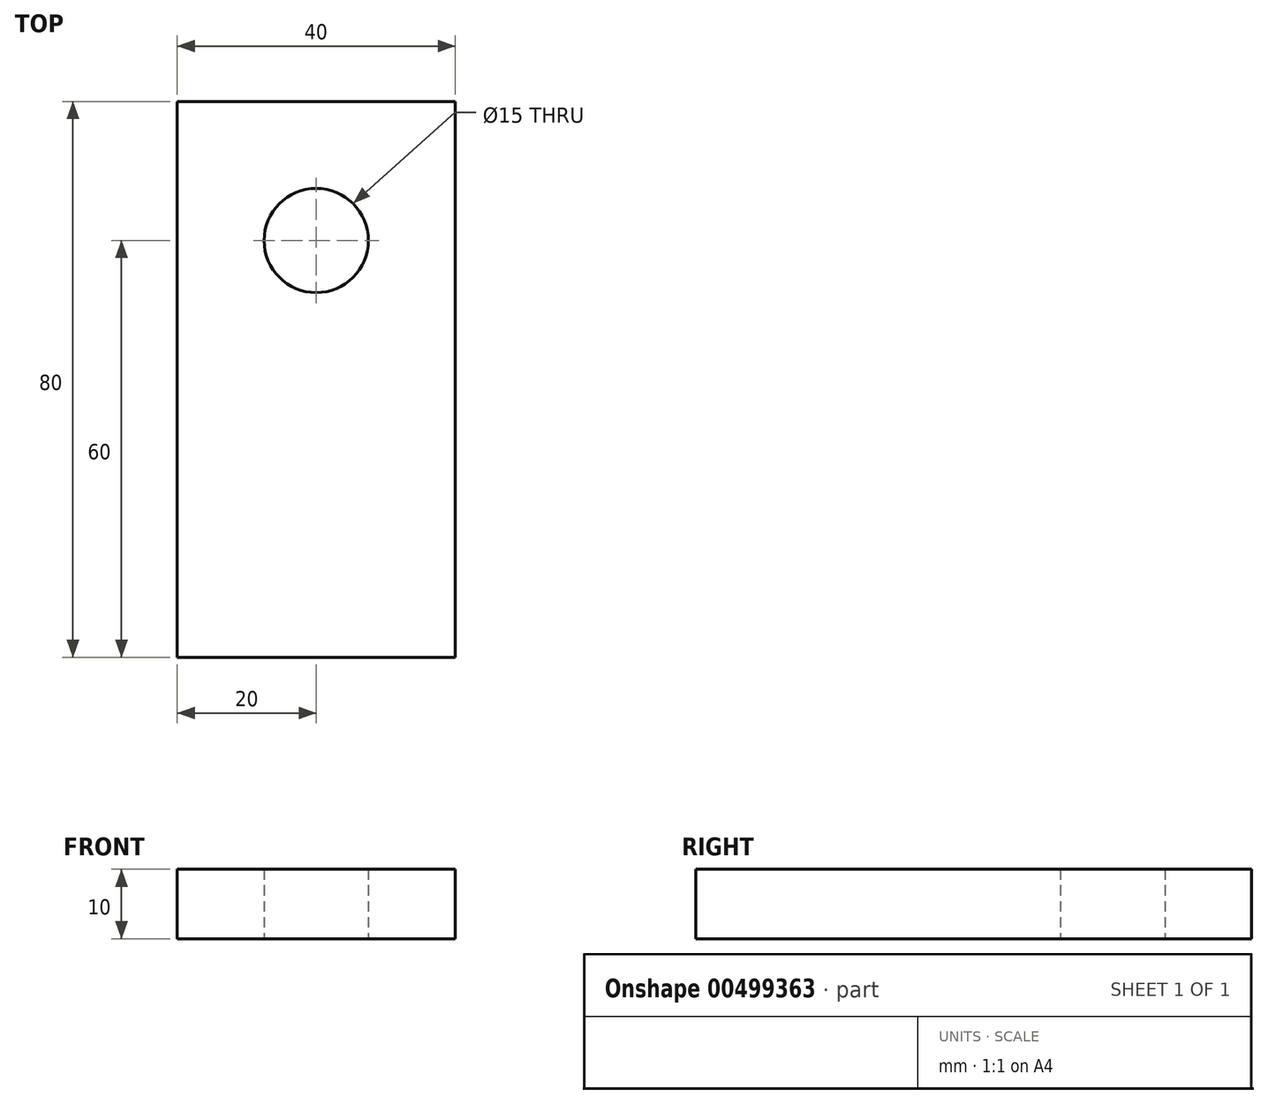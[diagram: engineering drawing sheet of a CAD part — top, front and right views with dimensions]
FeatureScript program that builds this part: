
annotation { "Feature Type Name" : "Feature", "Feature Type Description" : "" }
export const myFeature = defineFeature(function(context is Context, id is Id, definition is map)
    precondition{}
    {
        {
            var Q0;
            Q0=qCreatedBy(makeId("Top.planeOp"),FACE);
            var sketch = newSketch(context, id + "F0", { "sketchPlane" : qUnion([Q0])});
            skLineSegment(sketch, "E0.bottom", {"start": v(0, 0) * mm, "end": v(40, 0) * mm});
            skLineSegment(sketch, "E0.top", {"start": v(0, 80) * mm, "end": v(40, 80) * mm});
            skLineSegment(sketch, "E0.left", {"start": v(0, 0) * mm, "end": v(0, 80) * mm});
            skLineSegment(sketch, "E0.right", {"start": v(40, 0) * mm, "end": v(40, 80) * mm});
            skCircle(sketch, "E1", {"center": v(20, 60) * mm, "radius": 7.5 * mm});
            skSolve(sketch);
        }
        {
            var Q0;
            Q0 = qSketchRegion(id + "F0", true);
            extrude(context, id + "F1", {"entities" : qUnion([Q0]), "depth" : 10 * mm});
        }
    });
